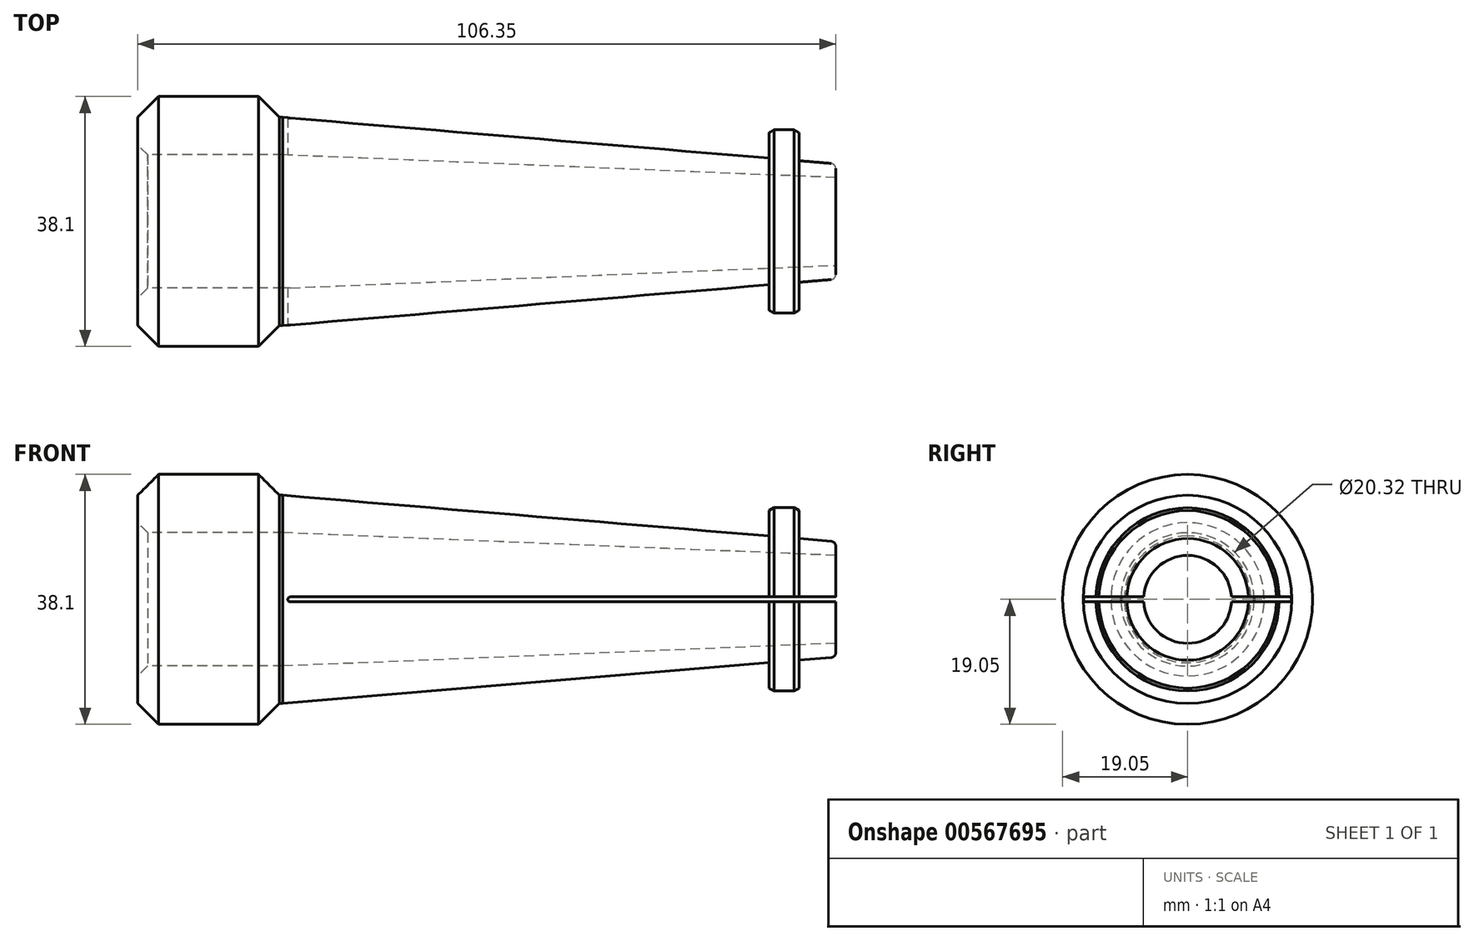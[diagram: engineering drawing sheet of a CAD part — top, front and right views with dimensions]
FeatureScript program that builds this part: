
annotation { "Feature Type Name" : "Feature", "Feature Type Description" : "" }
export const myFeature = defineFeature(function(context is Context, id is Id, definition is map)
    precondition{}
    {
        {
            var Q0;
            Q0=qCreatedBy(makeId("Front.planeOp"),FACE);
            var sketch = newSketch(context, id + "F0", { "sketchPlane" : qUnion([Q0])});
            skLineSegment(sketch, "E0", {"start": v(0, 0) * mm, "end": v(106.35, 0) * mm, "construction": true});
            skLineSegment(sketch, "E1", {"start": v(3.17, 19.05) * mm, "end": v(18.41, 19.05) * mm});
            skLineSegment(sketch, "E2", {"start": v(21.59, 15.88) * mm, "end": v(22.1, 15.88) * mm});
            skLineSegment(sketch, "E3", {"start": v(22.1, 15.88) * mm, "end": v(96.19, 9.65) * mm});
            skLineSegment(sketch, "E4", {"start": v(96.19, 9.65) * mm, "end": v(96.19, 13.97) * mm});
            skLineSegment(sketch, "E5", {"start": v(96.19, 13.97) * mm, "end": v(100.76, 13.97) * mm});
            skLineSegment(sketch, "E6", {"start": v(100.76, 13.97) * mm, "end": v(100.76, 9.27) * mm});
            skLineSegment(sketch, "E7", {"start": v(100.76, 9.27) * mm, "end": v(106.35, 8.8) * mm});
            skLineSegment(sketch, "E8", {"start": v(106.35, 0) * mm, "end": v(106.35, 8.8) * mm});
            skLineSegment(sketch, "E9", {"start": v(0, 10.16) * mm, "end": v(22.1, 10.16) * mm});
            skLineSegment(sketch, "E10", {"start": v(0, 10.16) * mm, "end": v(0, 15.87) * mm});
            skLineSegment(sketch, "E11", {"start": v(22.1, 10.16) * mm, "end": v(106.35, 6.7) * mm});
            skLineSegment(sketch, "E12", {"start": v(21.59, 15.88) * mm, "end": v(18.41, 19.05) * mm});
            skLineSegment(sketch, "E13", {"start": v(0, 15.87) * mm, "end": v(3.18, 19.05) * mm});
            skLineSegment(sketch, "E14.trimOffspring", {"start": v(18.53, 18.94) * mm, "end": v(20.88, 18.94) * mm});
            skSolve(sketch);
        }
        {
            var Q0;
            Q0 = qSketchRegion(id + "F0", true);
            var Q1;
            Q1=sQuery(id+"F0.wireOp",EDGE,"E0");
            revolve(context, id + "F1", {"entities" : qUnion([Q0]), "axis" : qUnion([Q1]), "revolveType" : RevolveType.FULL});
        }
        {
            var Q0;
            Q0=makeQuery(id+"F1.opRevolve","SWEPT_EDGE",EDGE,{"disambiguationData":[OSD([sQuery(id+"F0.wireOp",EDGE,"E5"),sQuery(id+"F0.wireOp",EDGE,"E6")])]});
            var Q1;
            Q1=makeQuery(id+"F1.opRevolve","SWEPT_EDGE",EDGE,{"disambiguationData":[OSD([sQuery(id+"F0.wireOp",EDGE,"E4"),sQuery(id+"F0.wireOp",EDGE,"E5")])]});
            chamfer(context, id + "F2", {"entities" : qUnion([Q0, Q1]), "chamferType" : ChamferType.OFFSET_ANGLE, "width" : 0.76 * mm, "oppositeDirection" : false, "angle" : 30 * degree, "tangentPropagation" : true});
        }
        {
            var Q0;
            Q0=makeQuery(id+"F1.opRevolve","SWEPT_EDGE",EDGE,{"disambiguationData":[OSD([sQuery(id+"F0.wireOp",EDGE,"E7"),sQuery(id+"F0.wireOp",EDGE,"E8")])]});
            fillet(context, id + "F3", {"entities" : qUnion([Q0]), "radius" : 0.76 * mm, "tangentPropagation" : true, "allowEdgeOverflow" : false});
        }
        {
            var Q0;
            Q0=makeQuery(id+"F1.opRevolve","SWEPT_EDGE",EDGE,{"disambiguationData":[OSD([sQuery(id+"F0.wireOp",EDGE,"E9"),sQuery(id+"F0.wireOp",EDGE,"E10")])]});
            chamfer(context, id + "F4", {"entities" : qUnion([Q0]), "chamferType" : ChamferType.OFFSET_ANGLE, "width" : 1.52 * mm, "oppositeDirection" : false, "angle" : 45 * degree, "tangentPropagation" : true});
        }
        {
            var Q0;
            Q0=qCreatedBy(makeId("Front.planeOp"),FACE);
            var sketch = newSketch(context, id + "F5", { "sketchPlane" : qUnion([Q0])});
            skArc(sketch, "E15", {"start": v(23.24, 0.38) * mm, "mid": v(22.86, 0) * mm, "end": v(23.24, -0.38) * mm});
            skLineSegment(sketch, "E16", {"start": v(23.24, 0.38) * mm, "end": v(107.36, 0.38) * mm});
            skLineSegment(sketch, "E17", {"start": v(23.22, -0.38) * mm, "end": v(107.36, -0.38) * mm});
            skLineSegment(sketch, "E18", {"start": v(107.36, 0.38) * mm, "end": v(107.36, -0.38) * mm});
            skSolve(sketch);
        }
        {
            var Q0;
            Q0 = qSketchRegion(id + "F5", true);
            extrude(context, id + "F6", {"entities" : qUnion([Q0]), "operationType" : NewBodyOperationType.REMOVE, "endBound" : BoundingType.SYMMETRIC, "oppositeDirection" : true, "depth" : 49.78 * mm, "offsetDistance" : 25.4 * mm});
        }
    });
